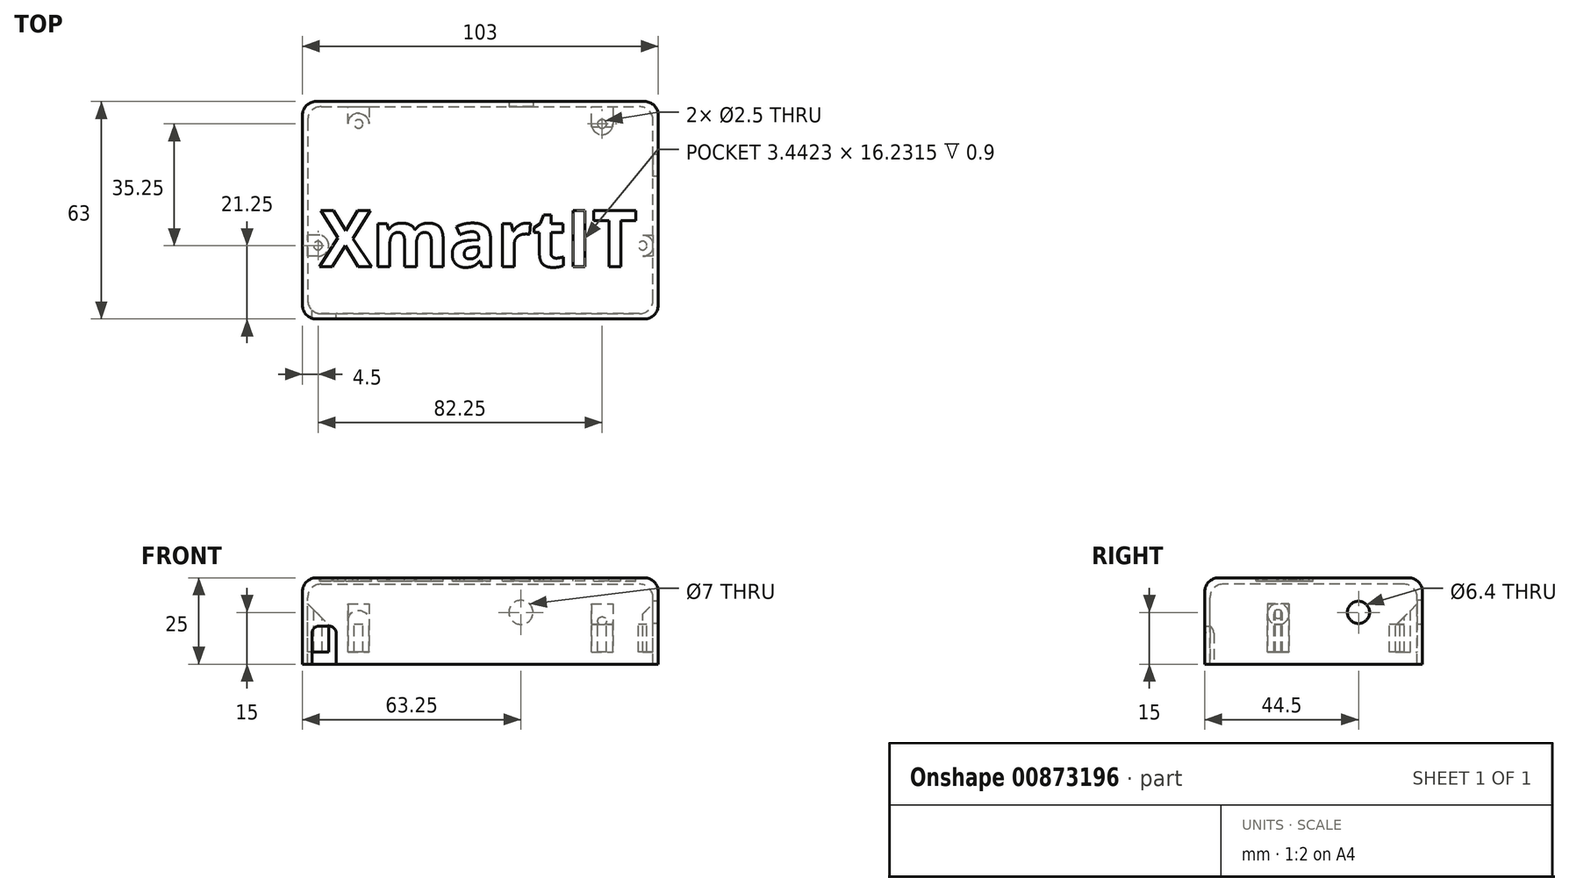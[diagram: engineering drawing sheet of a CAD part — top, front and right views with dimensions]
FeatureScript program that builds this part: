
annotation { "Feature Type Name" : "Feature", "Feature Type Description" : "" }
export const myFeature = defineFeature(function(context is Context, id is Id, definition is map)
    precondition{}
    {
        {
            assignVariable(context, id + "F0", {"name" : "Paredes", "anyValue" : 1.5});
        }
        {
            var Q0;
            Q0=qCreatedBy(makeId("Top.planeOp"),FACE);
            var sketch = newSketch(context, id + "F1", { "sketchPlane" : qUnion([Q0])});
            skLineSegment(sketch, "E0.bottom", {"start": v(50, -30) * mm, "end": v(-50, -30) * mm});
            skLineSegment(sketch, "E0.top", {"start": v(50, 30) * mm, "end": v(-50, 30) * mm});
            skLineSegment(sketch, "E0.left", {"start": v(50, -30) * mm, "end": v(50, 30) * mm});
            skLineSegment(sketch, "E0.right", {"start": v(-50, -30) * mm, "end": v(-50, 30) * mm});
            skPoint(sketch, "E0.middle", {"position": v(0, 0) * mm});
            skLineSegment(sketch, "E1.bottom", {"start": v(51.5, -31.5) * mm, "end": v(-51.5, -31.5) * mm});
            skLineSegment(sketch, "E1.top", {"start": v(51.5, 31.5) * mm, "end": v(-51.5, 31.5) * mm});
            skLineSegment(sketch, "E1.left", {"start": v(51.5, -31.5) * mm, "end": v(51.5, 31.5) * mm});
            skLineSegment(sketch, "E1.right", {"start": v(-51.5, -31.5) * mm, "end": v(-51.5, 31.5) * mm});
            skLineSegment(sketch, "E2.bottom", {"start": v(72.1, -40) * mm, "end": v(-72.1, -40) * mm});
            skLineSegment(sketch, "E2.top", {"start": v(72.1, 40) * mm, "end": v(-72.1, 40) * mm});
            skLineSegment(sketch, "E2.left", {"start": v(72.1, -40) * mm, "end": v(72.1, 40) * mm});
            skLineSegment(sketch, "E2.right", {"start": v(-72.1, -40) * mm, "end": v(-72.1, 40) * mm});
            skLineSegment(sketch, "E3", {"start": v(-51.5, 31.5) * mm, "end": v(-51.5, 40) * mm});
            skLineSegment(sketch, "E4", {"start": v(-51.5, -31.5) * mm, "end": v(-51.5, -40) * mm});
            skLineSegment(sketch, "E5", {"start": v(-41.73, -30) * mm, "end": v(-41.73, -4) * mm, "construction": true});
            skLineSegment(sketch, "E6.bottom", {"start": v(-50, -4) * mm, "end": v(50, -4) * mm});
            skLineSegment(sketch, "E6.top", {"start": v(-50, -2.2) * mm, "end": v(50, -2.2) * mm});
            skLineSegment(sketch, "E6.left", {"start": v(-50, -4) * mm, "end": v(-50, -2.2) * mm});
            skLineSegment(sketch, "E6.right", {"start": v(50, -4) * mm, "end": v(50, -2.2) * mm});
            skLineSegment(sketch, "E7.bottom", {"start": v(-55.7, -5) * mm, "end": v(-51.5, -5) * mm});
            skLineSegment(sketch, "E7.top", {"start": v(-55.7, 5) * mm, "end": v(-51.5, 5) * mm});
            skLineSegment(sketch, "E7.left", {"start": v(-55.7, -5) * mm, "end": v(-55.7, 5) * mm});
            skPoint(sketch, "E7.middle", {"position": v(-51.5, 0) * mm});
            skPoint(sketch, "E7.right.start.orphan", {"position": v(-47.3, -5) * mm});
            skPoint(sketch, "E8.trimOffspring.end.orphan", {"position": v(-47.3, 5) * mm});
            skLineSegment(sketch, "E9.bottom", {"start": v(72.1, -40) * mm, "end": v(84.1, -40) * mm});
            skLineSegment(sketch, "E9.top", {"start": v(72.1, -28) * mm, "end": v(84.1, -28) * mm});
            skLineSegment(sketch, "E9.left", {"start": v(72.1, -40) * mm, "end": v(72.1, -28) * mm});
            skLineSegment(sketch, "E9.right", {"start": v(87.1, -37) * mm, "end": v(87.1, -31) * mm});
            skCircle(sketch, "E10", {"center": v(79.6, -34) * mm, "radius": 1.5 * mm});
            skPoint(sketch, "E10.centerSnap0", {"position": v(87.1, -34) * mm});
            skPoint(sketch, "E10.centerSnap1", {"position": v(79.6, -28) * mm});
            skPoint(sketch, "E11.visualSharp", {"position": v(87.1, -28) * mm});
            skArc(sketch, "E11.filletArc", {"start": v(87.1, -31) * mm, "mid": v(86.22, -28.88) * mm, "end": v(84.1, -28) * mm});
            skPoint(sketch, "E12.visualSharp", {"position": v(87.1, -40) * mm});
            skArc(sketch, "E12.filletArc", {"start": v(84.1, -40) * mm, "mid": v(86.22, -39.12) * mm, "end": v(87.1, -37) * mm});
            skLineSegment(sketch, "E13", {"start": v(0, 0) * mm, "end": v(11.58, 0) * mm, "construction": true});
            skLineSegment(sketch, "E14.MirrorCS", {"start": v(87.1, 37) * mm, "end": v(87.1, 31) * mm});
            skPoint(sketch, "E15.MirrorP", {"position": v(79.6, 28) * mm});
            skCircle(sketch, "E16.MirrorC", {"center": v(79.6, 34) * mm, "radius": 1.5 * mm});
            skLineSegment(sketch, "E17.MirrorCS", {"start": v(72.1, 28) * mm, "end": v(84.1, 28) * mm});
            skPoint(sketch, "E18.MirrorP", {"position": v(87.1, 28) * mm});
            skArc(sketch, "E19.MirrorCS", {"start": v(87.1, 31) * mm, "mid": v(86.22, 28.88) * mm, "end": v(84.1, 28) * mm});
            skPoint(sketch, "E20.MirrorP", {"position": v(87.1, 40) * mm});
            skLineSegment(sketch, "E21.MirrorCS", {"start": v(72.1, 40) * mm, "end": v(84.1, 40) * mm});
            skPoint(sketch, "E22.MirrorP", {"position": v(87.1, 34) * mm});
            skArc(sketch, "E23.MirrorCS", {"start": v(84.1, 40) * mm, "mid": v(86.22, 39.12) * mm, "end": v(87.1, 37) * mm});
            skLineSegment(sketch, "E24", {"start": v(0, 31.5) * mm, "end": v(0, 40) * mm});
            skLineSegment(sketch, "E25", {"start": v(16, -31.5) * mm, "end": v(16, -38.7) * mm});
            skLineSegment(sketch, "E26", {"start": v(16, -38.7) * mm, "end": v(-51.5, -38.7) * mm});
            skLineSegment(sketch, "E27", {"start": v(16, -38.7) * mm, "end": v(16, -40) * mm});
            skSolve(sketch);
        }
        {
            var Q0;
            {var subQ10=sQuery(id+"F1.wireOp",EDGE,"E0.bottom");Q0=makeQuery(id+"F1.imprint","IMPRINT",FACE,{"disambiguationData":[TD([[makeQuery(id+"F1.imprint","IMPRINT",EDGE,{"derivedFrom":subQ10}),1.0]])]});}
            extrude(context, id + "F2", {"entities" : qUnion([Q0]), "oppositeDirection" : true, "depth" : 25 * mm, "offsetDistance" : 25 * mm});
        }
        {
            var Q0;
            {var subQ0=sQuery(id+"F1.wireOp",EDGE,"E0.bottom");Q0=makeQuery(id+"F1.imprint","IMPRINT",FACE,{"disambiguationData":[TD([[makeQuery(id+"F1.imprint","IMPRINT",EDGE,{"derivedFrom":subQ0}),-1.0]])]});}
            var Q1;
            {var subQ10=sQuery(id+"F1.wireOp",EDGE,"E0.bottom");Q1=makeQuery(id+"F1.imprint","IMPRINT",FACE,{"disambiguationData":[TD([[makeQuery(id+"F1.imprint","IMPRINT",EDGE,{"derivedFrom":subQ10}),1.0]])]});}
            var Q2;
            {var subQ0=sQuery(id+"F1.wireOp",EDGE,"E0.top");Q2=makeQuery(id+"F1.imprint","IMPRINT",FACE,{"disambiguationData":[TD([[makeQuery(id+"F1.imprint","IMPRINT",EDGE,{"derivedFrom":subQ0}),1.0]])]});}
            var Q3;
            {var subQ2=sQuery(id+"F1.wireOp",EDGE,"E6.bottom");Q3=makeQuery(id+"F1.imprint","IMPRINT",FACE,{"disambiguationData":[TD([[makeQuery(id+"F1.imprint","IMPRINT",EDGE,{"derivedFrom":subQ2}),1.0]])]});}
            extrude(context, id + "F3", {"entities" : qUnion([Q0, Q1, Q2, Q3]), "operationType" : NewBodyOperationType.ADD, "oppositeDirection" : true, "depth" : 1.8 * mm, "offsetDistance" : 25 * mm});
        }
        {
            var Q0;
            Q0=makeQuery(id+"F2.opExtrude","SWEPT_FACE",FACE,{"disambiguationData":[OSD([sQuery(id+"F1.wireOp",EDGE,"E1.left")])]});
            cPlane(context, id + "F4", {"entities" : qUnion([Q0]), "cplaneType" : CPlaneType.OFFSET, "offset" : (getVariable(context, 'Paredes')) * mm, "oppositeDirection" : true, "width" : 150 * mm, "height" : 150 * mm});
        }
        {
            var Q0;
            Q0=qCreatedBy(id+"F4.planeOp",FACE);
            var sketch = newSketch(context, id + "F5", { "sketchPlane" : qUnion([Q0])});
            skLineSegment(sketch, "E28", {"start": v(0, 0) * mm, "end": v(0, -10) * mm, "construction": true});
            skLineSegment(sketch, "E29", {"start": v(0, -10) * mm, "end": v(13, -10) * mm, "construction": true});
            skCircle(sketch, "E30", {"center": v(13, -10) * mm, "radius": 3.2 * mm});
            skCircle(sketch, "E31", {"center": v(13, -10) * mm, "radius": 4.75 * mm});
            skSolve(sketch);
        }
        {
            var Q0;
            Q0=makeQuery(id+"F5.imprint","IMPRINT",FACE,{"disambiguationData":[TD([[makeQuery(id+"F5.imprint","IMPRINT",EDGE,{"derivedFrom":sQuery(id+"F5.wireOp",EDGE,"E30")}),1.0]])]});
            var Q1;
            Q1=makeQuery(id+"F2.opExtrude","SWEPT_FACE",FACE,{"disambiguationData":[OSD([sQuery(id+"F1.wireOp",EDGE,"E1.left")])]});
            extrude(context, id + "F6", {"entities" : qUnion([Q0]), "operationType" : NewBodyOperationType.REMOVE, "endBound" : BoundingType.UP_TO_NEXT, "depth" : 35 * mm, "endBoundEntityFace" : qUnion([Q1]), "offsetDistance" : 10 * mm, "offsetOppositeDirection" : true});
        }
        {
            var Q0;
            Q0=makeQuery(id+"F5.imprint","IMPRINT",FACE,{"disambiguationData":[TD([[makeQuery(id+"F5.imprint","IMPRINT",EDGE,{"derivedFrom":sQuery(id+"F5.wireOp",EDGE,"E30")}),-1.0]])]});
            var Q1;
            Q1=makeQuery(id+"F5.imprint","IMPRINT",FACE,{"disambiguationData":[TD([[makeQuery(id+"F5.imprint","IMPRINT",EDGE,{"derivedFrom":sQuery(id+"F5.wireOp",EDGE,"E30")}),1.0]])]});
            extrude(context, id + "F7", {"entities" : qUnion([Q0, Q1]), "operationType" : NewBodyOperationType.REMOVE, "oppositeDirection" : true, "depth" : 35 * mm, "offsetDistance" : 25 * mm});
        }
        {
            var Q0;
            Q0=qCreatedBy(makeId("Front.planeOp"),FACE);
            var sketch = newSketch(context, id + "F8", { "sketchPlane" : qUnion([Q0])});
            skLineSegment(sketch, "E32", {"start": v(0, 0) * mm, "end": v(0, -10) * mm, "construction": true});
            skLineSegment(sketch, "E33", {"start": v(0, -10) * mm, "end": v(11.75, -10) * mm, "construction": true});
            skCircle(sketch, "E34", {"center": v(11.75, -10) * mm, "radius": 3.5 * mm});
            skCircle(sketch, "E35.MirrorC", {"center": v(-11.75, -10) * mm, "radius": 3.5 * mm});
            skLineSegment(sketch, "E36", {"start": v(-11.75, -10) * mm, "end": v(-35.25, -10) * mm, "construction": true});
            skCircle(sketch, "E37", {"center": v(-35.25, -10) * mm, "radius": 3.5 * mm});
            skLineSegment(sketch, "E38", {"start": v(-35.25, -10) * mm, "end": v(-38.75, -10) * mm, "construction": true});
            skLineSegment(sketch, "E39", {"start": v(-38.75, -10) * mm, "end": v(-41.75, -10) * mm, "construction": true});
            skLineSegment(sketch, "E40", {"start": v(-41.75, -10) * mm, "end": v(-41.75, -14) * mm, "construction": true});
            skLineSegment(sketch, "E41.bottom", {"start": v(-41.75, -14) * mm, "end": v(-48.75, -14) * mm});
            skLineSegment(sketch, "E41.top", {"start": v(-41.75, -25) * mm, "end": v(-48.75, -25) * mm});
            skLineSegment(sketch, "E41.left", {"start": v(-41.75, -14) * mm, "end": v(-41.75, -25) * mm});
            skLineSegment(sketch, "E41.right", {"start": v(-48.75, -14) * mm, "end": v(-48.75, -25) * mm});
            skCircle(sketch, "E42.MirrorC", {"center": v(35.25, -10) * mm, "radius": 3.5 * mm});
            skSolve(sketch);
        }
        {
            var Q0;
            Q0=makeQuery(id+"F8.imprint","IMPRINT",FACE,{"disambiguationData":[TD([[makeQuery(id+"F8.imprint","IMPRINT",EDGE,{"derivedFrom":sQuery(id+"F8.wireOp",EDGE,"E34")}),1.0]])]});
            var Q1;
            Q1=makeQuery(id+"F8.imprint","IMPRINT",FACE,{"disambiguationData":[TD([[makeQuery(id+"F8.imprint","IMPRINT",EDGE,{"derivedFrom":sQuery(id+"F8.wireOp",EDGE,"E35.MirrorC")}),-1.0]])]});
            extrude(context, id + "F9", {"entities" : qUnion([Q0, Q1]), "operationType" : NewBodyOperationType.REMOVE, "endBound" : BoundingType.THROUGH_ALL, "oppositeDirection" : true, "depth" : 25 * mm, "offsetDistance" : 25 * mm});
        }
        {
            var Q0;
            Q0=makeQuery(id+"F8.imprint","IMPRINT",FACE,{"disambiguationData":[TD([[makeQuery(id+"F8.imprint","IMPRINT",EDGE,{"derivedFrom":sQuery(id+"F8.wireOp",EDGE,"E41.bottom")}),1.0]])]});
            extrude(context, id + "F10", {"entities" : qUnion([Q0]), "operationType" : NewBodyOperationType.REMOVE, "endBound" : BoundingType.THROUGH_ALL, "depth" : 25 * mm, "offsetDistance" : 25 * mm});
        }
        {
            var Q0;
            Q0=makeQuery(id+"F10.boolean.opBoolean","COPY",EDGE,{"derivedFrom":makeQuery(id+"F10.opExtrude","SWEPT_EDGE",EDGE,{"disambiguationData":[OSD([sQuery(id+"F8.wireOp",EDGE,"E41.bottom"),sQuery(id+"F8.wireOp",EDGE,"E41.right")])]})});
            var Q1;
            Q1=makeQuery(id+"F10.boolean.opBoolean","COPY",EDGE,{"derivedFrom":makeQuery(id+"F10.opExtrude","SWEPT_EDGE",EDGE,{"disambiguationData":[OSD([sQuery(id+"F8.wireOp",EDGE,"E41.bottom"),sQuery(id+"F8.wireOp",EDGE,"E41.left")])]})});
            fillet(context, id + "F11", {"entities" : qUnion([Q0, Q1]), "radius" : 2 * mm, "tangentPropagation" : true, "allowEdgeOverflow" : false});
        }
        {
            var Q0;
            {var subQ0=sQuery(id+"F1.wireOp",EDGE,"E1.right");var subQ1=sQuery(id+"F1.wireOp",EDGE,"E1.left");var subQ2=sQuery(id+"F1.wireOp",EDGE,"E1.top");var subQ3=sQuery(id+"F1.wireOp",EDGE,"E1.bottom");Q0=makeQuery(id+"F3.boolean.opBoolean","MERGE",FACE,{"derivedFrom":[makeQuery(id+"F2.opExtrude","CAP_FACE",FACE,{"disambiguationData":[OSD([sQuery(id+"F1.wireOp",EDGE,"E0.bottom"),sQuery(id+"F1.wireOp",EDGE,"E0.top"),sQuery(id+"F1.wireOp",EDGE,"E0.left"),sQuery(id+"F1.wireOp",EDGE,"E0.right"),subQ3,subQ2,subQ1,subQ0])],"isStart":true}),makeQuery(id+"F3.opExtrude","CAP_FACE",FACE,{"disambiguationData":[OSD([subQ3,subQ2,subQ1,subQ0])],"isStart":true})]});}
            cPlane(context, id + "F12", {"entities" : qUnion([Q0]), "cplaneType" : CPlaneType.OFFSET, "offset" : 13.5 * mm, "oppositeDirection" : true, "width" : 150 * mm, "height" : 150 * mm});
        }
        {
            var Q0;
            Q0=qCreatedBy(id+"F12.planeOp",FACE);
            var sketch = newSketch(context, id + "F13", { "sketchPlane" : qUnion([Q0])});
            skLineSegment(sketch, "E43", {"start": v(0, 0) * mm, "end": v(0, 0) * mm});
            skLineSegment(sketch, "E44", {"start": v(0, 0) * mm, "end": v(0, 1.5) * mm, "construction": true});
            skCircle(sketch, "E45", {"center": v(0, 1.5) * mm, "radius": 1.25 * mm});
            skCircle(sketch, "E46", {"center": v(0, 1.5) * mm, "radius": 3.1 * mm});
            skCircle(sketch, "E47.0.1.0", {"center": v(0, 13.25) * mm, "radius": 3.1 * mm});
            skCircle(sketch, "E47.0.1.1", {"center": v(0, 13.25) * mm, "radius": 1.25 * mm});
            skCircle(sketch, "E47.0.2.0", {"center": v(0, 25) * mm, "radius": 3.1 * mm});
            skCircle(sketch, "E47.0.2.1", {"center": v(0, 25) * mm, "radius": 1.25 * mm});
            skCircle(sketch, "E47.1.0.0", {"center": v(11.75, 1.5) * mm, "radius": 3.1 * mm});
            skCircle(sketch, "E47.1.0.1", {"center": v(11.75, 1.5) * mm, "radius": 1.25 * mm});
            skCircle(sketch, "E47.1.1.0", {"center": v(11.75, 13.25) * mm, "radius": 3.1 * mm});
            skCircle(sketch, "E47.1.1.1", {"center": v(11.75, 13.25) * mm, "radius": 1.25 * mm});
            skCircle(sketch, "E47.1.2.0", {"center": v(11.75, 25) * mm, "radius": 3.1 * mm});
            skCircle(sketch, "E47.1.2.1", {"center": v(11.75, 25) * mm, "radius": 1.25 * mm});
            skCircle(sketch, "E47.2.0.0", {"center": v(23.5, 1.5) * mm, "radius": 3.1 * mm});
            skCircle(sketch, "E47.2.0.1", {"center": v(23.5, 1.5) * mm, "radius": 1.25 * mm});
            skCircle(sketch, "E47.2.1.0", {"center": v(23.5, 13.25) * mm, "radius": 3.1 * mm});
            skCircle(sketch, "E47.2.1.1", {"center": v(23.5, 13.25) * mm, "radius": 1.25 * mm});
            skCircle(sketch, "E47.2.2.0", {"center": v(23.5, 25) * mm, "radius": 3.1 * mm});
            skCircle(sketch, "E47.2.2.1", {"center": v(23.5, 25) * mm, "radius": 1.25 * mm});
            skCircle(sketch, "E47.3.0.0", {"center": v(35.25, 1.5) * mm, "radius": 3.1 * mm});
            skCircle(sketch, "E47.3.0.1", {"center": v(35.25, 1.5) * mm, "radius": 1.25 * mm});
            skCircle(sketch, "E47.3.1.0", {"center": v(35.25, 13.25) * mm, "radius": 3.1 * mm});
            skCircle(sketch, "E47.3.1.1", {"center": v(35.25, 13.25) * mm, "radius": 1.25 * mm});
            skCircle(sketch, "E47.3.2.0", {"center": v(35.25, 25) * mm, "radius": 3.1 * mm});
            skCircle(sketch, "E47.3.2.1", {"center": v(35.25, 25) * mm, "radius": 1.25 * mm});
            skCircle(sketch, "E47.4.0.0", {"center": v(47, 1.5) * mm, "radius": 3.1 * mm});
            skCircle(sketch, "E47.4.0.1", {"center": v(47, 1.5) * mm, "radius": 1.25 * mm});
            skCircle(sketch, "E47.4.1.0", {"center": v(47, 13.25) * mm, "radius": 3.1 * mm});
            skCircle(sketch, "E47.4.1.1", {"center": v(47, 13.25) * mm, "radius": 1.25 * mm});
            skCircle(sketch, "E47.4.2.0", {"center": v(47, 25) * mm, "radius": 3.1 * mm});
            skCircle(sketch, "E47.4.2.1", {"center": v(47, 25) * mm, "radius": 1.25 * mm});
            skLineSegment(sketch, "E47.direction1", {"start": v(0, 1.5) * mm, "end": v(11.75, 1.5) * mm, "construction": true});
            skLineSegment(sketch, "E47.direction2", {"start": v(0, 1.5) * mm, "end": v(0, 13.25) * mm, "construction": true});
            skCircle(sketch, "E48.MirrorC", {"center": v(-11.75, 1.5) * mm, "radius": 1.25 * mm});
            skCircle(sketch, "E49.MirrorC", {"center": v(-35.25, 25) * mm, "radius": 1.25 * mm});
            skCircle(sketch, "E50.MirrorC", {"center": v(-47, 25) * mm, "radius": 1.25 * mm});
            skCircle(sketch, "E51.MirrorC", {"center": v(-11.75, 25) * mm, "radius": 1.25 * mm});
            skCircle(sketch, "E52.MirrorC", {"center": v(-47, 1.5) * mm, "radius": 1.25 * mm});
            skCircle(sketch, "E53.MirrorC", {"center": v(-47, 13.25) * mm, "radius": 1.25 * mm});
            skCircle(sketch, "E54.MirrorC", {"center": v(-11.75, 13.25) * mm, "radius": 1.25 * mm});
            skCircle(sketch, "E55.MirrorC", {"center": v(-23.5, 25) * mm, "radius": 1.25 * mm});
            skCircle(sketch, "E56.MirrorC", {"center": v(-23.5, 1.5) * mm, "radius": 1.25 * mm});
            skCircle(sketch, "E57.MirrorC", {"center": v(-35.25, 1.5) * mm, "radius": 1.25 * mm});
            skCircle(sketch, "E58.MirrorC", {"center": v(-35.25, 13.25) * mm, "radius": 1.25 * mm});
            skCircle(sketch, "E59.MirrorC", {"center": v(-23.5, 13.25) * mm, "radius": 1.25 * mm});
            skCircle(sketch, "E60.MirrorC", {"center": v(-11.75, 13.25) * mm, "radius": 3.1 * mm});
            skCircle(sketch, "E61.MirrorC", {"center": v(-35.25, 25) * mm, "radius": 3.1 * mm});
            skCircle(sketch, "E62.MirrorC", {"center": v(-47, 25) * mm, "radius": 3.1 * mm});
            skCircle(sketch, "E63.MirrorC", {"center": v(-35.25, 1.5) * mm, "radius": 3.1 * mm});
            skCircle(sketch, "E64.MirrorC", {"center": v(-47, 13.25) * mm, "radius": 3.1 * mm});
            skCircle(sketch, "E65.MirrorC", {"center": v(-23.5, 25) * mm, "radius": 3.1 * mm});
            skCircle(sketch, "E66.MirrorC", {"center": v(-11.75, 1.5) * mm, "radius": 3.1 * mm});
            skCircle(sketch, "E67.MirrorC", {"center": v(-35.25, 13.25) * mm, "radius": 3.1 * mm});
            skCircle(sketch, "E68.MirrorC", {"center": v(-47, 1.5) * mm, "radius": 3.1 * mm});
            skCircle(sketch, "E69.MirrorC", {"center": v(-11.75, 25) * mm, "radius": 3.1 * mm});
            skCircle(sketch, "E70.MirrorC", {"center": v(-23.5, 1.5) * mm, "radius": 3.1 * mm});
            skCircle(sketch, "E71.MirrorC", {"center": v(-23.5, 13.25) * mm, "radius": 3.1 * mm});
            skCircle(sketch, "E72.MirrorC", {"center": v(-47, -10.25) * mm, "radius": 3.1 * mm});
            skCircle(sketch, "E73.MirrorC", {"center": v(-47, -10.25) * mm, "radius": 1.25 * mm});
            skLineSegment(sketch, "E74", {"start": v(-47, -10.25) * mm, "end": v(-47, -7.15) * mm, "construction": true});
            skLineSegment(sketch, "E75", {"start": v(-47, -7.15) * mm, "end": v(-50.1, -7.15) * mm});
            skLineSegment(sketch, "E76", {"start": v(-47, -10.25) * mm, "end": v(-50.1, -10.25) * mm, "construction": true});
            skLineSegment(sketch, "E77", {"start": v(-50.1, -10.25) * mm, "end": v(-50.1, -7.15) * mm});
            skLineSegment(sketch, "E78.MirrorCS", {"start": v(-47, -13.35) * mm, "end": v(-50.1, -13.35) * mm});
            skLineSegment(sketch, "E79.MirrorCS", {"start": v(-50.1, -10.25) * mm, "end": v(-50.1, -13.35) * mm});
            skLineSegment(sketch, "E80", {"start": v(35.25, 25) * mm, "end": v(32.15, 25) * mm, "construction": true});
            skLineSegment(sketch, "E81", {"start": v(32.15, 25) * mm, "end": v(32.15, 30.06) * mm});
            skLineSegment(sketch, "E82", {"start": v(32.15, 30.06) * mm, "end": v(38.35, 30.06) * mm});
            skLineSegment(sketch, "E83", {"start": v(35.25, 25) * mm, "end": v(38.35, 25) * mm, "construction": true});
            skLineSegment(sketch, "E84", {"start": v(38.35, 25) * mm, "end": v(38.35, 30.06) * mm});
            skLineSegment(sketch, "E85", {"start": v(-47, -10.25) * mm, "end": v(-43.9, -10.25) * mm, "construction": true});
            skLineSegment(sketch, "E86", {"start": v(-43.9, -10.25) * mm, "end": v(-39.9, -10.25) * mm, "construction": true});
            skLineSegment(sketch, "E87", {"start": v(-39.9, -10.25) * mm, "end": v(-39.9, -30.05) * mm});
            skLineSegment(sketch, "E88", {"start": v(-39.9, -30.05) * mm, "end": v(-38.1, -30.05) * mm});
            skLineSegment(sketch, "E89", {"start": v(-38.1, -30.05) * mm, "end": v(-38.1, -10.25) * mm});
            skLineSegment(sketch, "E90", {"start": v(-38.1, -10.25) * mm, "end": v(-39.9, -10.25) * mm});
            skLineSegment(sketch, "E91.MirrorCS", {"start": v(-32.15, 25) * mm, "end": v(-32.15, 30.06) * mm});
            skLineSegment(sketch, "E92.MirrorCS", {"start": v(-38.35, 25) * mm, "end": v(-38.35, 30.06) * mm});
            skCircle(sketch, "E93.MirrorC", {"center": v(47, -10.25) * mm, "radius": 3.1 * mm});
            skLineSegment(sketch, "E94.MirrorCS", {"start": v(47, -13.35) * mm, "end": v(50.1, -13.35) * mm});
            skLineSegment(sketch, "E95.MirrorCS", {"start": v(47, -7.15) * mm, "end": v(50.1, -7.15) * mm});
            skCircle(sketch, "E96.MirrorC", {"center": v(47, -10.25) * mm, "radius": 1.25 * mm});
            skLineSegment(sketch, "E97.MirrorCS", {"start": v(-32.15, 30.06) * mm, "end": v(-38.35, 30.06) * mm});
            skLineSegment(sketch, "E98.MirrorCS", {"start": v(50.1, -10.25) * mm, "end": v(50.1, -13.35) * mm});
            skLineSegment(sketch, "E99.MirrorCS", {"start": v(50.1, -10.25) * mm, "end": v(50.1, -7.15) * mm});
            skSolve(sketch);
        }
        {
            var Q0;
            Q0=makeQuery(id+"F13.imprint","IMPRINT",FACE,{"disambiguationData":[TD([[makeQuery(id+"F13.imprint","IMPRINT",EDGE,{"derivedFrom":sQuery(id+"F13.wireOp",EDGE,"E47.3.2.0")}),1.0]])]});
            var Q1;
            {var subQ0=sQuery(id+"F13.wireOp",EDGE,"E81");Q1=makeQuery(id+"F13.imprint","IMPRINT",FACE,{"disambiguationData":[TD([[makeQuery(id+"F13.imprint","IMPRINT",EDGE,{"derivedFrom":subQ0}),-1.0]])]});}
            var Q2;
            {var subQ0=sQuery(id+"F13.wireOp",EDGE,"E91.MirrorCS");Q2=makeQuery(id+"F13.imprint","IMPRINT",FACE,{"disambiguationData":[TD([[makeQuery(id+"F13.imprint","IMPRINT",EDGE,{"derivedFrom":subQ0}),1.0]])]});}
            var Q3;
            Q3=makeQuery(id+"F13.imprint","IMPRINT",FACE,{"disambiguationData":[TD([[makeQuery(id+"F13.imprint","IMPRINT",EDGE,{"derivedFrom":sQuery(id+"F13.wireOp",EDGE,"E49.MirrorC")}),1.0]])]});
            var Q4;
            {var subQ2=sQuery(id+"F13.wireOp",EDGE,"E78.MirrorCS");Q4=makeQuery(id+"F13.imprint","IMPRINT",FACE,{"disambiguationData":[TD([[makeQuery(id+"F13.imprint","IMPRINT",EDGE,{"derivedFrom":subQ2}),-1.0]])]});}
            var Q5;
            Q5=makeQuery(id+"F13.imprint","IMPRINT",FACE,{"disambiguationData":[TD([[makeQuery(id+"F13.imprint","IMPRINT",EDGE,{"derivedFrom":sQuery(id+"F13.wireOp",EDGE,"E73.MirrorC")}),-1.0]])]});
            var Q6;
            {var subQ0=sQuery(id+"F13.wireOp",EDGE,"E75");Q6=makeQuery(id+"F13.imprint","IMPRINT",FACE,{"disambiguationData":[TD([[makeQuery(id+"F13.imprint","IMPRINT",EDGE,{"derivedFrom":subQ0}),1.0]])]});}
            var Q7;
            {var subQ0=sQuery(id+"F13.wireOp",EDGE,"E95.MirrorCS");Q7=makeQuery(id+"F13.imprint","IMPRINT",FACE,{"disambiguationData":[TD([[makeQuery(id+"F13.imprint","IMPRINT",EDGE,{"derivedFrom":subQ0}),-1.0]])]});}
            var Q8;
            Q8=makeQuery(id+"F13.imprint","IMPRINT",FACE,{"disambiguationData":[TD([[makeQuery(id+"F13.imprint","IMPRINT",EDGE,{"derivedFrom":sQuery(id+"F13.wireOp",EDGE,"E96.MirrorC")}),1.0]])]});
            var Q9;
            {var subQ0=sQuery(id+"F13.wireOp",EDGE,"E94.MirrorCS");Q9=makeQuery(id+"F13.imprint","IMPRINT",FACE,{"disambiguationData":[TD([[makeQuery(id+"F13.imprint","IMPRINT",EDGE,{"derivedFrom":subQ0}),1.0]])]});}
            extrude(context, id + "F14", {"entities" : qUnion([Q0, Q1, Q2, Q3, Q4, Q5, Q6, Q7, Q8, Q9]), "operationType" : NewBodyOperationType.ADD, "oppositeDirection" : true, "depth" : 8 * mm, "offsetDistance" : 25 * mm});
        }
        {
            var Q0;
            Q0=makeQuery(id+"F3.opExtrude","CAP_FACE",FACE,{"disambiguationData":[OSD([sQuery(id+"F1.wireOp",EDGE,"E1.bottom"),sQuery(id+"F1.wireOp",EDGE,"E1.top"),sQuery(id+"F1.wireOp",EDGE,"E1.left"),sQuery(id+"F1.wireOp",EDGE,"E1.right")])],"isStart":false});
            var Q1;
            {var subQ0=sQuery(id+"F1.wireOp",EDGE,"E1.right");var subQ1=sQuery(id+"F1.wireOp",EDGE,"E1.left");var subQ2=sQuery(id+"F1.wireOp",EDGE,"E1.top");var subQ3=sQuery(id+"F1.wireOp",EDGE,"E1.bottom");Q1=makeQuery(id+"F3.boolean.opBoolean","MERGE",FACE,{"derivedFrom":[makeQuery(id+"F2.opExtrude","CAP_FACE",FACE,{"disambiguationData":[OSD([sQuery(id+"F1.wireOp",EDGE,"E0.bottom"),sQuery(id+"F1.wireOp",EDGE,"E0.top"),sQuery(id+"F1.wireOp",EDGE,"E0.left"),sQuery(id+"F1.wireOp",EDGE,"E0.right"),subQ3,subQ2,subQ1,subQ0])],"isStart":true}),makeQuery(id+"F3.opExtrude","CAP_FACE",FACE,{"disambiguationData":[OSD([subQ3,subQ2,subQ1,subQ0])],"isStart":true})]});}
            var Q2;
            Q2=makeQuery(id+"F2.opExtrude","SWEPT_EDGE",EDGE,{"disambiguationData":[OSD([sQuery(id+"F1.wireOp",EDGE,"E1.bottom"),sQuery(id+"F1.wireOp",EDGE,"E1.left")])]});
            var Q3;
            Q3=makeQuery(id+"F2.opExtrude","SWEPT_EDGE",EDGE,{"disambiguationData":[OSD([sQuery(id+"F1.wireOp",EDGE,"E1.top"),sQuery(id+"F1.wireOp",EDGE,"E1.left")])]});
            var Q4;
            Q4=makeQuery(id+"F2.opExtrude","SWEPT_EDGE",EDGE,{"disambiguationData":[OSD([sQuery(id+"F1.wireOp",EDGE,"E1.bottom"),sQuery(id+"F1.wireOp",EDGE,"E1.right"),sQuery(id+"F1.wireOp",EDGE,"E4")])]});
            var Q5;
            Q5=makeQuery(id+"F2.opExtrude","SWEPT_EDGE",EDGE,{"disambiguationData":[OSD([sQuery(id+"F1.wireOp",EDGE,"E1.top"),sQuery(id+"F1.wireOp",EDGE,"E1.right"),sQuery(id+"F1.wireOp",EDGE,"E3")])]});
            var Q6;
            Q6=makeQuery(id+"F2.opExtrude","SWEPT_EDGE",EDGE,{"disambiguationData":[OSD([sQuery(id+"F1.wireOp",EDGE,"E0.top"),sQuery(id+"F1.wireOp",EDGE,"E0.left")])]});
            var Q7;
            Q7=makeQuery(id+"F2.opExtrude","SWEPT_EDGE",EDGE,{"disambiguationData":[OSD([sQuery(id+"F1.wireOp",EDGE,"E0.top"),sQuery(id+"F1.wireOp",EDGE,"E0.right")])]});
            var Q8;
            Q8=makeQuery(id+"F2.opExtrude","SWEPT_EDGE",EDGE,{"disambiguationData":[OSD([sQuery(id+"F1.wireOp",EDGE,"E0.bottom"),sQuery(id+"F1.wireOp",EDGE,"E0.right")])]});
            var Q9;
            Q9=makeQuery(id+"F2.opExtrude","SWEPT_EDGE",EDGE,{"disambiguationData":[OSD([sQuery(id+"F1.wireOp",EDGE,"E0.bottom"),sQuery(id+"F1.wireOp",EDGE,"E0.left")])]});
            fillet(context, id + "F15", {"entities" : qUnion([Q0, Q1, Q2, Q3, Q4, Q5, Q6, Q7, Q8, Q9]), "radius" : 4 * mm, "tangentPropagation" : true, "allowEdgeOverflow" : false});
        }
        {
            var Q0;
            Q0=qCreatedBy(makeId("Top.planeOp"),FACE);
            var sketch = newSketch(context, id + "F16", { "sketchPlane" : qUnion([Q0])});
            skText(sketch, "E100", { "text": "XmartIT", "fontName": "OpenSans-Bold.ttf"});
            const initialGuessF16  = {"E100": [-0.04658, -0.01637, 1, 0, 0.01637]};
            skSetInitialGuess(sketch, initialGuessF16);
            skSolve(sketch);
        }
        {
            var Q0;
            Q0 = qSketchRegion(id + "F16", true);
            extrude(context, id + "F17", {"entities" : qUnion([Q0]), "operationType" : NewBodyOperationType.REMOVE, "oppositeDirection" : true, "depth" : 0.9 * mm, "offsetDistance" : 25 * mm});
        }
        {
            var Q0;
            Q0=makeQuery(id+"F14.boolean.opBoolean","INTERSECT",EDGE,{"derivedFrom":[makeQuery(id+"F2.opExtrude","SWEPT_FACE",FACE,{"disambiguationData":[OSD([sQuery(id+"F1.wireOp",EDGE,"E0.left")])]}),makeQuery(id+"F14.opExtrude","CAP_FACE",FACE,{"disambiguationData":[OSD([sQuery(id+"F13.wireOp",EDGE,"E93.MirrorC"),sQuery(id+"F13.wireOp",EDGE,"E94.MirrorCS"),sQuery(id+"F13.wireOp",EDGE,"E95.MirrorCS"),sQuery(id+"F13.wireOp",EDGE,"E96.MirrorC"),sQuery(id+"F13.wireOp",EDGE,"E98.MirrorCS"),sQuery(id+"F13.wireOp",EDGE,"E99.MirrorCS")])],"isStart":true})]});
            var Q1;
            Q1=makeQuery(id+"F14.boolean.opBoolean","INTERSECT",EDGE,{"derivedFrom":[makeQuery(id+"F2.opExtrude","SWEPT_FACE",FACE,{"disambiguationData":[OSD([sQuery(id+"F1.wireOp",EDGE,"E0.right")])]}),makeQuery(id+"F14.opExtrude","CAP_FACE",FACE,{"disambiguationData":[OSD([sQuery(id+"F13.wireOp",EDGE,"E72.MirrorC"),sQuery(id+"F13.wireOp",EDGE,"E73.MirrorC"),sQuery(id+"F13.wireOp",EDGE,"E75"),sQuery(id+"F13.wireOp",EDGE,"E77"),sQuery(id+"F13.wireOp",EDGE,"E78.MirrorCS"),sQuery(id+"F13.wireOp",EDGE,"E79.MirrorCS")])],"isStart":true})]});
            var Q2;
            Q2=makeQuery(id+"F14.boolean.opBoolean","INTERSECT",EDGE,{"derivedFrom":[makeQuery(id+"F2.opExtrude","SWEPT_FACE",FACE,{"disambiguationData":[OSD([sQuery(id+"F1.wireOp",EDGE,"E0.top")])]}),makeQuery(id+"F14.opExtrude","CAP_FACE",FACE,{"disambiguationData":[OSD([sQuery(id+"F13.wireOp",EDGE,"E49.MirrorC"),sQuery(id+"F13.wireOp",EDGE,"E61.MirrorC"),sQuery(id+"F13.wireOp",EDGE,"E91.MirrorCS"),sQuery(id+"F13.wireOp",EDGE,"E92.MirrorCS"),sQuery(id+"F13.wireOp",EDGE,"E97.MirrorCS")])],"isStart":true})]});
            var Q3;
            Q3=makeQuery(id+"F14.boolean.opBoolean","INTERSECT",EDGE,{"derivedFrom":[makeQuery(id+"F2.opExtrude","SWEPT_FACE",FACE,{"disambiguationData":[OSD([sQuery(id+"F1.wireOp",EDGE,"E0.top")])]}),makeQuery(id+"F14.opExtrude","CAP_FACE",FACE,{"disambiguationData":[OSD([sQuery(id+"F13.wireOp",EDGE,"E47.3.2.0"),sQuery(id+"F13.wireOp",EDGE,"E47.3.2.1"),sQuery(id+"F13.wireOp",EDGE,"E81"),sQuery(id+"F13.wireOp",EDGE,"E82"),sQuery(id+"F13.wireOp",EDGE,"E84")])],"isStart":true})]});
            chamfer(context, id + "F18", {"entities" : qUnion([Q0, Q1, Q2, Q3]), "width" : 6 * mm, "tangentPropagation" : true});
        }
    });
